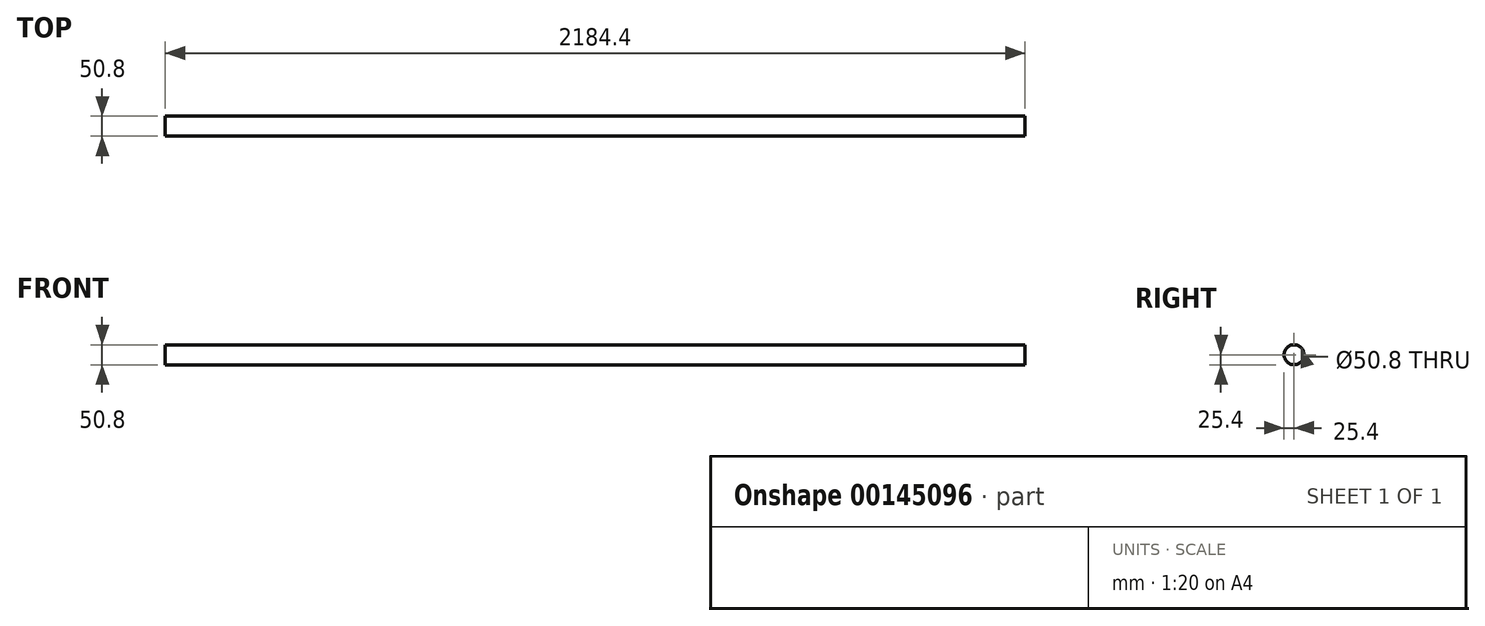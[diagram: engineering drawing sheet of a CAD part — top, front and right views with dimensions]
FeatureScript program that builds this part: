
annotation { "Feature Type Name" : "Feature", "Feature Type Description" : "" }
export const myFeature = defineFeature(function(context is Context, id is Id, definition is map)
    precondition{}
    {
        {
            var Q0;
            Q0=qCreatedBy(makeId("Top.planeOp"),FACE);
            var sketch = newSketch(context, id + "F0", { "sketchPlane" : qUnion([Q0])});
            skLineSegment(sketch, "E0", {"start": v(-1109.27, 0) * mm, "end": v(1075.13, 0) * mm});
            skArc(sketch, "E1", {"start": v(1075.13, 0) * mm, "mid": v(1160.8, 26.36) * mm, "end": v(1216.84, 96.32) * mm});
            skArc(sketch, "E2", {"start": v(-1109.27, 0) * mm, "mid": v(-1200.27, 30.15) * mm, "end": v(-1255.26, 108.68) * mm});
            skLineSegment(sketch, "E3.0", {"start": v(-1110.71, -25.4) * mm, "end": v(1075.13, -25.4) * mm});
            skArc(sketch, "E4.0", {"start": v(1073.84, -25.4) * mm, "mid": v(1178.62, 7.83) * mm, "end": v(1243.85, 96.3) * mm});
            skLineSegment(sketch, "E5", {"start": v(1216.84, 96.32) * mm, "end": v(1270.44, 96.32) * mm});
            skArc(sketch, "E6.0", {"start": v(-1110.47, -25.4) * mm, "mid": v(-1218.92, 12.44) * mm, "end": v(-1281.6, 108.68) * mm});
            skLineSegment(sketch, "E7", {"start": v(-1255.26, 108.68) * mm, "end": v(-1307.82, 108.68) * mm});
            skArc(sketch, "E8.0", {"start": v(1073.65, -50.8) * mm, "mid": v(1196.8, -10.35) * mm, "end": v(1270.44, 96.32) * mm});
            skPoint(sketch, "E9.orphan", {"position": v(1243.85, 96.32) * mm});
            skArc(sketch, "E10.0", {"start": v(-1110.64, -50.8) * mm, "mid": v(-1237.1, -5.56) * mm, "end": v(-1307.7, 108.68) * mm});
            skSolve(sketch);
        }
        {
            var Q0;
            Q0=sQuery(id+"F0.wireOp",EDGE,"E0");
            var Q1;
            Q1=sQuery(id+"F0.wireOp",EDGE,"E3.0");
            revolve(context, id + "F1", {"bodyType" : ToolBodyType.SURFACE, "surfaceEntities" : qUnion([Q0]), "axis" : qUnion([Q1]), "revolveType" : RevolveType.FULL});
        }
    });
